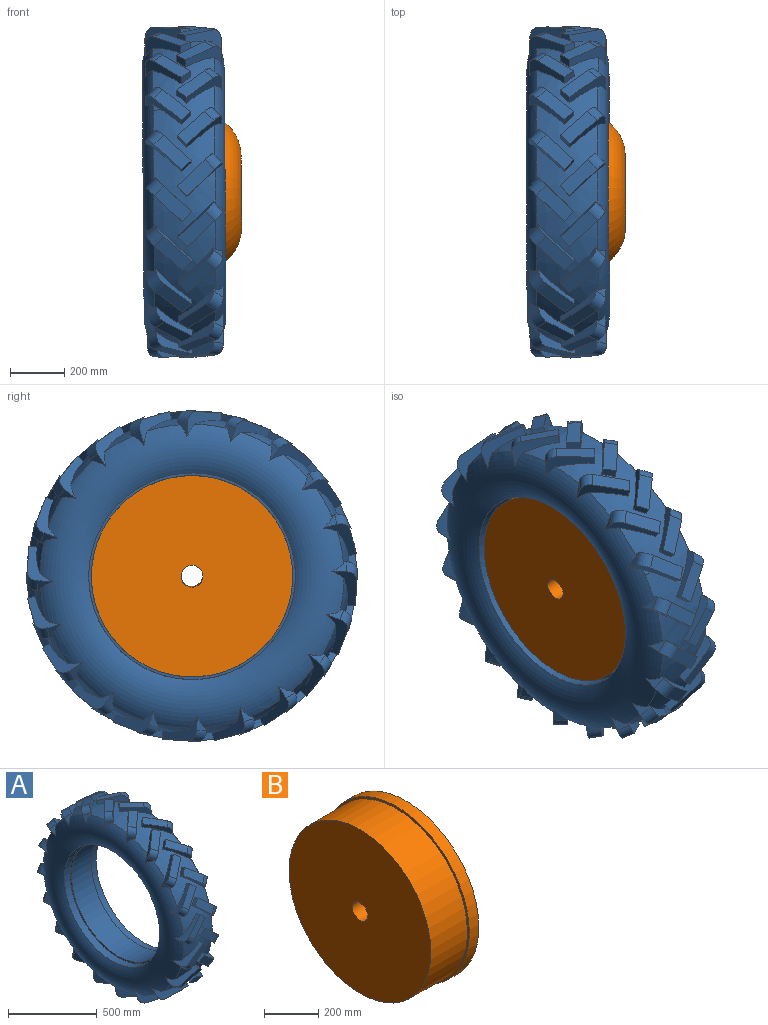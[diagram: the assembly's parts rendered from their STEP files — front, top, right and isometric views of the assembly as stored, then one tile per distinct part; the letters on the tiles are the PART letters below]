
ASSEMBLY  parts=2 mates=2
PART A: 250 faces, bbox 300.1x1226.5x1226.5 mm
  f0: torus R=460mm, axis (-1,0,0), area 542471mm2, adj f2,f4,f7,f8,f19,f20,f31,f32
  f1: cylinder r=370mm len=740mm, axis (1,0,0), area 371964.6mm2, adj f247,f249
  f2: torus R=270mm, axis (-1,0,0), area 493305.8mm2, adj f0,f3,f4,f5,f6,f7,f8,f9
  f3: torus R=270mm, axis (-1,0,0), area 381.1mm2, adj f2,f5,f195
  f4: torus R=270mm, axis (-1,0,0), area 29.1mm2, adj f0,f2,f175
  f5: torus R=460mm, axis (-1,0,0), area 542472mm2, adj f2,f3,f14,f15,f26,f27,f38,f39
  f6: plane 130.79x120.93mm, normal (0.69,0.11,-0.72), area 5311.1mm2, adj f2,f7,f9,f10,f11
  f7: plane 52.38x44.2mm, normal (-0.73,0.11,-0.68), area 1246mm2, adj f0,f2,f6,f8,f11
  f8: plane 130.8x121.4mm, normal (-0.69,-0.11,0.72), area 7014.7mm2, adj f0,f2,f7,f9,f10,f11
  f9: plane 40.79x34.46mm, normal (0.73,-0.11,0.68), area 1433.2mm2, adj f2,f6,f8,f10
  f10: plane 136.08x130.89mm, normal (0,-0.99,-0.16), area 7000mm2, adj f6,f8,f9,f11
  f11: cylinder r=40mm len=63.42mm, axis (0.69,0.11,-0.72), area 3141.6mm2, adj f6,f7,f8,f10
  f12: plane 36.44x34.46mm, normal (-0.73,0,0.69), area 1433.2mm2, adj f2,f13,f15,f16
  f13: plane 130.79x123.67mm, normal (-0.69,0,-0.73), area 5311.1mm2, adj f2,f12,f14,f16,f17
  f14: plane 53.02x36.34mm, normal (0.73,0,-0.69), area 1245.9mm2, adj f2,f5,f13,f15,f17
  f15: plane 130.79x123.67mm, normal (0.69,0,0.73), area 7014.7mm2, adj f2,f5,f12,f14,f16,f17
  f16: plane 136.08x132.52mm, normal (0,-1,0), area 7000mm2, adj f12,f13,f15,f17
  f17: cylinder r=40mm len=63.81mm, axis (-0.69,0,-0.73), area 3141.6mm2, adj f13,f14,f15,f16
  f18: plane 130.79x110.59mm, normal (0.69,0.33,-0.65), area 5311.1mm2, adj f2,f19,f21,f22,f23
  f19: plane 56.47x47.26mm, normal (-0.73,0.31,-0.61), area 1246mm2, adj f0,f2,f18,f20,f23
  f20: plane 139.03x130.8mm, normal (-0.69,-0.33,0.65), area 7014.7mm2, adj f0,f2,f19,f21,f22,f23
  f21: plane 46.41x41.26mm, normal (0.73,-0.31,0.61), area 1433.2mm2, adj f2,f18,f20,f22
  f22: plane 136.08x118.07mm, normal (0,-0.89,-0.45), area 7000mm2, adj f18,f20,f21,f23
  f23: cylinder r=40mm len=64.61mm, axis (0.69,0.33,-0.65), area 3141.6mm2, adj f18,f19,f20,f22
  f24: plane 44.15x37.65mm, normal (-0.73,-0.21,0.65), area 1433.2mm2, adj f2,f25,f27,f28
  f25: plane 130.79x116.58mm, normal (-0.69,0.22,-0.69), area 5311.1mm2, adj f2,f24,f26,f28,f29
  f26: plane 50.94x50.42mm, normal (0.73,0.21,-0.65), area 1245.9mm2, adj f2,f5,f25,f27,f29
  f27: plane 130.79x126.67mm, normal (0.69,-0.22,0.69), area 7014.7mm2, adj f2,f5,f24,f26,f28,f29
  f28: plane 136.08x126.03mm, normal (0,-0.95,-0.31), area 7000mm2, adj f24,f25,f27,f29
  f29: cylinder r=40mm len=63.42mm, axis (-0.69,0.22,-0.69), area 3141.6mm2, adj f25,f26,f27,f28
  f30: plane 130.79x122.3mm, normal (0.69,0.51,-0.51), area 5311.1mm2, adj f2,f31,f33,f34,f35
  f31: plane 63.2x37.51mm, normal (-0.73,0.49,-0.49), area 1245.9mm2, adj f0,f2,f30,f32,f35
  f32: plane 153.23x130.8mm, normal (-0.69,-0.51,0.51), area 7014.7mm2, adj f0,f2,f31,f33,f34,f35
  f33: plane 47.5x45.37mm, normal (0.73,-0.49,0.49), area 1433.2mm2, adj f2,f30,f32,f34
  f34: plane 136.08x93.7mm, normal (0,-0.71,-0.71), area 7000mm2, adj f30,f32,f33,f35
  f35: cylinder r=40mm len=73.41mm, axis (0.69,0.51,-0.51), area 3141.6mm2, adj f30,f31,f32,f34
  f36: plane 47.54x43.85mm, normal (-0.73,-0.4,0.56), area 1433.2mm2, adj f2,f37,f39,f40
  f37: plane 130.79x112.57mm, normal (-0.69,0.43,-0.59), area 5311.1mm2, adj f2,f36,f38,f40,f41
  f38: plane 60.56x42.89mm, normal (0.73,0.4,-0.56), area 1245.9mm2, adj f2,f5,f37,f39,f41
  f39: plane 147.94x130.79mm, normal (0.69,-0.43,0.59), area 7014.7mm2, adj f2,f5,f36,f38,f40,f41
  f40: plane 136.08x107.21mm, normal (0,-0.81,-0.59), area 7000mm2, adj f36,f37,f39,f41
  f41: cylinder r=40mm len=69.87mm, axis (-0.69,0.43,-0.59), area 3141.6mm2, adj f37,f38,f39,f40
  f42: plane 132.57x130.79mm, normal (0.69,0.65,-0.33), area 5311.1mm2, adj f2,f43,f45,f46,f47
  f43: plane 63.75x36.6mm, normal (-0.73,0.61,-0.31), area 1245.9mm2, adj f0,f2,f42,f44,f47
  f44: plane 152.43x130.81mm, normal (-0.69,-0.65,0.33), area 7014.7mm2, adj f0,f2,f43,f45,f46,f47
  f45: plane 45.04x43.94mm, normal (0.73,-0.61,0.31), area 1433.2mm2, adj f2,f42,f44,f46
  f46: plane 136.08x118.07mm, normal (0,-0.45,-0.89), area 7000mm2, adj f42,f44,f45,f47
  f47: cylinder r=40mm len=75.02mm, axis (0.69,0.65,-0.33), area 3141.6mm2, adj f42,f43,f44,f46
  f48: plane 46.29x45.77mm, normal (-0.73,-0.56,0.4), area 1433.2mm2, adj f2,f49,f51,f52
  f49: plane 130.79x129.02mm, normal (-0.69,0.59,-0.43), area 5311.1mm2, adj f2,f48,f50,f52,f53
  f50: plane 64.25x34.86mm, normal (0.73,0.56,-0.4), area 1245.9mm2, adj f2,f5,f49,f51,f53
  f51: plane 154.72x130.79mm, normal (0.69,-0.59,0.43), area 7014.7mm2, adj f2,f5,f48,f50,f52,f53
  f52: plane 136.08x107.21mm, normal (0,-0.59,-0.81), area 7000mm2, adj f48,f49,f51,f53
  f53: cylinder r=40mm len=75.14mm, axis (-0.69,0.59,-0.43), area 3141.6mm2, adj f49,f50,f51,f52
  f54: plane 130.79x129.86mm, normal (0.69,0.72,-0.11), area 5311.1mm2, adj f2,f55,f57,f58,f59
  f55: plane 58.07x37.35mm, normal (-0.73,0.68,-0.11), area 1245.9mm2, adj f0,f2,f54,f56,f59
  f56: plane 136.72x130.81mm, normal (-0.69,-0.72,0.11), area 7014.7mm2, adj f0,f2,f55,f57,f58,f59
  f57: plane 40.32x36.1mm, normal (0.73,-0.68,0.11), area 1433.2mm2, adj f2,f54,f56,f58
  f58: plane 136.08x130.89mm, normal (0,-0.16,-0.99), area 7000mm2, adj f54,f56,f57,f59
  f59: cylinder r=40mm len=69.28mm, axis (0.69,0.72,-0.11), area 3141.6mm2, adj f54,f55,f56,f58
  f60: plane 43.21x40.52mm, normal (-0.73,-0.65,0.21), area 1433.2mm2, adj f2,f61,f63,f64
  f61: plane 132.85x130.79mm, normal (-0.69,0.69,-0.22), area 5311.1mm2, adj f2,f60,f62,f64,f65
  f62: plane 61.65x37.43mm, normal (0.73,0.65,-0.21), area 1245.9mm2, adj f2,f5,f61,f63,f65
  f63: plane 146.36x130.79mm, normal (0.69,-0.69,0.22), area 7014.7mm2, adj f2,f5,f60,f62,f64,f65
  f64: plane 136.08x126.03mm, normal (0,-0.31,-0.95), area 7000mm2, adj f60,f61,f63,f65
  f65: cylinder r=40mm len=73.05mm, axis (-0.69,0.69,-0.22), area 3141.6mm2, adj f61,f62,f63,f64
  f66: plane 130.79x120.93mm, normal (0.69,0.72,0.11), area 5311.1mm2, adj f2,f67,f69,f70,f71
  f67: plane 52.38x44.2mm, normal (-0.73,0.68,0.11), area 1246mm2, adj f0,f2,f66,f68,f71
  f68: plane 130.8x121.4mm, normal (-0.69,-0.72,-0.11), area 7014.7mm2, adj f0,f2,f67,f69,f70,f71
  f69: plane 40.79x34.46mm, normal (0.73,-0.68,-0.11), area 1433.2mm2, adj f2,f66,f68,f70
  f70: plane 136.08x130.89mm, normal (0,0.16,-0.99), area 7000mm2, adj f66,f68,f69,f71
  f71: cylinder r=40mm len=63.42mm, axis (0.69,0.72,0.11), area 3141.6mm2, adj f66,f67,f68,f70
  f72: plane 36.44x34.46mm, normal (-0.73,-0.69,0), area 1433.2mm2, adj f2,f73,f75,f76
  f73: plane 130.79x123.67mm, normal (-0.69,0.73,0), area 5311.1mm2, adj f2,f72,f74,f76,f77
  f74: plane 53.02x36.34mm, normal (0.73,0.69,0), area 1245.9mm2, adj f2,f5,f73,f75,f77
  f75: plane 130.79x123.67mm, normal (0.69,-0.73,0), area 7014.7mm2, adj f2,f5,f72,f74,f76,f77
  f76: plane 136.08x132.52mm, normal (0,0,-1), area 7000mm2, adj f72,f73,f75,f77
  f77: cylinder r=40mm len=63.81mm, axis (-0.69,0.73,0), area 3141.6mm2, adj f73,f74,f75,f76
  f78: plane 130.79x110.59mm, normal (0.69,0.65,0.33), area 5311.1mm2, adj f2,f79,f81,f82,f83
  f79: plane 56.47x47.26mm, normal (-0.73,0.61,0.31), area 1246mm2, adj f0,f2,f78,f80,f83
  f80: plane 139.03x130.8mm, normal (-0.69,-0.65,-0.33), area 7014.7mm2, adj f0,f2,f79,f81,f82,f83
  f81: plane 46.41x41.26mm, normal (0.73,-0.61,-0.31), area 1433.2mm2, adj f2,f78,f80,f82
  f82: plane 136.08x118.07mm, normal (0,0.45,-0.89), area 7000mm2, adj f78,f80,f81,f83
  f83: cylinder r=40mm len=64.61mm, axis (0.69,0.65,0.33), area 3141.6mm2, adj f78,f79,f80,f82
  f84: plane 44.15x37.65mm, normal (-0.73,-0.65,-0.21), area 1433.2mm2, adj f2,f85,f87,f88
  f85: plane 130.79x116.58mm, normal (-0.69,0.69,0.22), area 5311.1mm2, adj f2,f84,f86,f88,f89
  f86: plane 50.94x50.42mm, normal (0.73,0.65,0.21), area 1245.9mm2, adj f2,f5,f85,f87,f89
  f87: plane 130.79x126.67mm, normal (0.69,-0.69,-0.22), area 7014.7mm2, adj f2,f5,f84,f86,f88,f89
  f88: plane 136.08x126.03mm, normal (0,0.31,-0.95), area 7000mm2, adj f84,f85,f87,f89
  f89: cylinder r=40mm len=63.42mm, axis (-0.69,0.69,0.22), area 3141.6mm2, adj f85,f86,f87,f88
  f90: plane 130.79x122.3mm, normal (0.69,0.51,0.51), area 5311.1mm2, adj f2,f91,f93,f94,f95
  f91: plane 63.2x37.51mm, normal (-0.73,0.49,0.49), area 1245.9mm2, adj f0,f2,f90,f92,f95
  f92: plane 153.23x130.8mm, normal (-0.69,-0.51,-0.51), area 7014.7mm2, adj f0,f2,f91,f93,f94,f95
  f93: plane 47.5x45.37mm, normal (0.73,-0.49,-0.49), area 1433.2mm2, adj f2,f90,f92,f94
  f94: plane 136.08x93.7mm, normal (0,0.71,-0.71), area 7000mm2, adj f90,f92,f93,f95
  f95: cylinder r=40mm len=73.41mm, axis (0.69,0.51,0.51), area 3141.6mm2, adj f90,f91,f92,f94
  f96: plane 47.54x43.85mm, normal (-0.73,-0.56,-0.4), area 1433.2mm2, adj f2,f97,f99,f100
  f97: plane 130.79x112.57mm, normal (-0.69,0.59,0.43), area 5311.1mm2, adj f2,f96,f98,f100,f101
  f98: plane 60.56x42.89mm, normal (0.73,0.56,0.4), area 1245.9mm2, adj f2,f5,f97,f99,f101
  f99: plane 147.94x130.79mm, normal (0.69,-0.59,-0.43), area 7014.7mm2, adj f2,f5,f96,f98,f100,f101
  f100: plane 136.08x107.21mm, normal (0,0.59,-0.81), area 7000mm2, adj f96,f97,f99,f101
  f101: cylinder r=40mm len=69.87mm, axis (-0.69,0.59,0.43), area 3141.6mm2, adj f97,f98,f99,f100
  f102: plane 132.57x130.79mm, normal (0.69,0.33,0.65), area 5311.1mm2, adj f2,f103,f105,f106,f107
  f103: plane 63.75x36.6mm, normal (-0.73,0.31,0.61), area 1245.9mm2, adj f0,f2,f102,f104,f107
  f104: plane 152.43x130.81mm, normal (-0.69,-0.33,-0.65), area 7014.7mm2, adj f0,f2,f103,f105,f106,f107
  f105: plane 45.04x43.94mm, normal (0.73,-0.31,-0.61), area 1433.2mm2, adj f2,f102,f104,f106
  f106: plane 136.08x118.07mm, normal (0,0.89,-0.45), area 7000mm2, adj f102,f104,f105,f107
  f107: cylinder r=40mm len=75.02mm, axis (0.69,0.33,0.65), area 3141.6mm2, adj f102,f103,f104,f106
  f108: plane 46.29x45.77mm, normal (-0.73,-0.4,-0.56), area 1433.2mm2, adj f2,f109,f111,f112
  f109: plane 130.79x129.02mm, normal (-0.69,0.43,0.59), area 5311.1mm2, adj f2,f108,f110,f112,f113
  f110: plane 64.25x34.86mm, normal (0.73,0.4,0.56), area 1245.9mm2, adj f2,f5,f109,f111,f113
  f111: plane 154.72x130.79mm, normal (0.69,-0.43,-0.59), area 7014.7mm2, adj f2,f5,f108,f110,f112,f113
  f112: plane 136.08x107.21mm, normal (0,0.81,-0.59), area 7000mm2, adj f108,f109,f111,f113
  f113: cylinder r=40mm len=75.14mm, axis (-0.69,0.43,0.59), area 3141.6mm2, adj f109,f110,f111,f112
  f114: plane 130.79x129.86mm, normal (0.69,0.11,0.72), area 5311.1mm2, adj f2,f115,f117,f118,f119
  f115: plane 58.07x37.35mm, normal (-0.73,0.11,0.68), area 1245.9mm2, adj f0,f2,f114,f116,f119
  f116: plane 136.72x130.81mm, normal (-0.69,-0.11,-0.72), area 7014.7mm2, adj f0,f2,f115,f117,f118,f119
  f117: plane 40.32x36.1mm, normal (0.73,-0.11,-0.68), area 1433.2mm2, adj f2,f114,f116,f118
  f118: plane 136.08x130.89mm, normal (0,0.99,-0.16), area 7000mm2, adj f114,f116,f117,f119
  f119: cylinder r=40mm len=69.28mm, axis (0.69,0.11,0.72), area 3141.6mm2, adj f114,f115,f116,f118
  f120: plane 43.21x40.52mm, normal (-0.73,-0.21,-0.65), area 1433.2mm2, adj f2,f121,f123,f124
  f121: plane 132.85x130.79mm, normal (-0.69,0.22,0.69), area 5311.1mm2, adj f2,f120,f122,f124,f125
  f122: plane 61.65x37.43mm, normal (0.73,0.21,0.65), area 1245.9mm2, adj f2,f5,f121,f123,f125
  f123: plane 146.36x130.79mm, normal (0.69,-0.22,-0.69), area 7014.7mm2, adj f2,f5,f120,f122,f124,f125
  f124: plane 136.08x126.03mm, normal (0,0.95,-0.31), area 7000mm2, adj f120,f121,f123,f125
  f125: cylinder r=40mm len=73.05mm, axis (-0.69,0.22,0.69), area 3141.6mm2, adj f121,f122,f123,f124
  f126: plane 130.79x120.93mm, normal (0.69,-0.11,0.72), area 5311.1mm2, adj f2,f127,f129,f130,f131
  f127: plane 52.38x44.2mm, normal (-0.73,-0.11,0.68), area 1246mm2, adj f0,f2,f126,f128,f131
  f128: plane 130.8x121.4mm, normal (-0.69,0.11,-0.72), area 7014.7mm2, adj f0,f2,f127,f129,f130,f131
  f129: plane 40.79x34.46mm, normal (0.73,0.11,-0.68), area 1433.2mm2, adj f2,f126,f128,f130
  f130: plane 136.08x130.89mm, normal (0,0.99,0.16), area 7000mm2, adj f126,f128,f129,f131
  f131: cylinder r=40mm len=63.42mm, axis (0.69,-0.11,0.72), area 3141.6mm2, adj f126,f127,f128,f130
  f132: plane 36.44x34.46mm, normal (-0.73,0,-0.69), area 1433.2mm2, adj f2,f133,f135,f136
  f133: plane 130.79x123.67mm, normal (-0.69,0,0.73), area 5311.1mm2, adj f2,f132,f134,f136,f137
  f134: plane 53.02x36.34mm, normal (0.73,0,0.69), area 1245.9mm2, adj f2,f5,f133,f135,f137
  f135: plane 130.79x123.67mm, normal (0.69,0,-0.73), area 7014.7mm2, adj f2,f5,f132,f134,f136,f137
  f136: plane 136.08x132.52mm, normal (0,1,0), area 7000mm2, adj f132,f133,f135,f137
  f137: cylinder r=40mm len=63.81mm, axis (-0.69,0,0.73), area 3141.6mm2, adj f133,f134,f135,f136
  f138: plane 130.79x110.59mm, normal (0.69,-0.33,0.65), area 5311.1mm2, adj f2,f139,f141,f142,f143
  f139: plane 56.47x47.26mm, normal (-0.73,-0.31,0.61), area 1246mm2, adj f0,f2,f138,f140,f143
  f140: plane 139.03x130.8mm, normal (-0.69,0.33,-0.65), area 7014.7mm2, adj f0,f2,f139,f141,f142,f143
  f141: plane 46.41x41.26mm, normal (0.73,0.31,-0.61), area 1433.2mm2, adj f2,f138,f140,f142
  f142: plane 136.08x118.07mm, normal (0,0.89,0.45), area 7000mm2, adj f138,f140,f141,f143
  f143: cylinder r=40mm len=64.61mm, axis (0.69,-0.33,0.65), area 3141.6mm2, adj f138,f139,f140,f142
  f144: plane 44.15x37.65mm, normal (-0.73,0.21,-0.65), area 1433.2mm2, adj f2,f145,f147,f148
  f145: plane 130.79x116.58mm, normal (-0.69,-0.22,0.69), area 5311.1mm2, adj f2,f144,f146,f148,f149
  f146: plane 50.94x50.42mm, normal (0.73,-0.21,0.65), area 1245.9mm2, adj f2,f5,f145,f147,f149
  f147: plane 130.79x126.67mm, normal (0.69,0.22,-0.69), area 7014.7mm2, adj f2,f5,f144,f146,f148,f149
  f148: plane 136.08x126.03mm, normal (0,0.95,0.31), area 7000mm2, adj f144,f145,f147,f149
  f149: cylinder r=40mm len=63.42mm, axis (-0.69,-0.22,0.69), area 3141.6mm2, adj f145,f146,f147,f148
  f150: plane 130.79x122.3mm, normal (0.69,-0.51,0.51), area 5311.1mm2, adj f2,f151,f153,f154,f155
  f151: plane 63.2x37.51mm, normal (-0.73,-0.49,0.49), area 1245.9mm2, adj f0,f2,f150,f152,f155
  f152: plane 153.23x130.8mm, normal (-0.69,0.51,-0.51), area 7014.7mm2, adj f0,f2,f151,f153,f154,f155
  f153: plane 47.5x45.37mm, normal (0.73,0.49,-0.49), area 1433.2mm2, adj f2,f150,f152,f154
  f154: plane 136.08x93.7mm, normal (0,0.71,0.71), area 7000mm2, adj f150,f152,f153,f155
  f155: cylinder r=40mm len=73.41mm, axis (0.69,-0.51,0.51), area 3141.6mm2, adj f150,f151,f152,f154
  f156: plane 47.54x43.85mm, normal (-0.73,0.4,-0.56), area 1433.2mm2, adj f2,f157,f159,f160
  f157: plane 130.79x112.57mm, normal (-0.69,-0.43,0.59), area 5311.1mm2, adj f2,f156,f158,f160,f161
  f158: plane 60.56x42.89mm, normal (0.73,-0.4,0.56), area 1245.9mm2, adj f2,f5,f157,f159,f161
  f159: plane 147.94x130.79mm, normal (0.69,0.43,-0.59), area 7014.7mm2, adj f2,f5,f156,f158,f160,f161
  f160: plane 136.08x107.21mm, normal (0,0.81,0.59), area 7000mm2, adj f156,f157,f159,f161
  f161: cylinder r=40mm len=69.87mm, axis (-0.69,-0.43,0.59), area 3141.6mm2, adj f157,f158,f159,f160
  f162: plane 132.57x130.79mm, normal (0.69,-0.65,0.33), area 5311.1mm2, adj f2,f163,f165,f166,f167
  f163: plane 63.75x36.6mm, normal (-0.73,-0.61,0.31), area 1245.9mm2, adj f0,f2,f162,f164,f167
  f164: plane 152.43x130.81mm, normal (-0.69,0.65,-0.33), area 7014.7mm2, adj f0,f2,f163,f165,f166,f167
  f165: plane 45.04x43.94mm, normal (0.73,0.61,-0.31), area 1433.2mm2, adj f2,f162,f164,f166
  f166: plane 136.08x118.07mm, normal (0,0.45,0.89), area 7000mm2, adj f162,f164,f165,f167
  f167: cylinder r=40mm len=75.02mm, axis (0.69,-0.65,0.33), area 3141.6mm2, adj f162,f163,f164,f166
  f168: plane 46.29x45.77mm, normal (-0.73,0.56,-0.4), area 1433.2mm2, adj f2,f169,f171,f172
  f169: plane 130.79x129.02mm, normal (-0.69,-0.59,0.43), area 5311.1mm2, adj f2,f168,f170,f172,f173
  f170: plane 64.25x34.86mm, normal (0.73,-0.56,0.4), area 1245.9mm2, adj f2,f5,f169,f171,f173
  f171: plane 154.72x130.79mm, normal (0.69,0.59,-0.43), area 7014.7mm2, adj f2,f5,f168,f170,f172,f173
  f172: plane 136.08x107.21mm, normal (0,0.59,0.81), area 7000mm2, adj f168,f169,f171,f173
  f173: cylinder r=40mm len=75.14mm, axis (-0.69,-0.59,0.43), area 3141.6mm2, adj f169,f170,f171,f172
  f174: plane 130.79x129.86mm, normal (0.69,-0.72,0.11), area 5311.1mm2, adj f2,f175,f177,f178,f179
  f175: plane 58.07x37.35mm, normal (-0.73,-0.68,0.11), area 1245.9mm2, adj f0,f4,f174,f176,f179
  f176: plane 136.72x130.81mm, normal (-0.69,0.72,-0.11), area 7014.7mm2, adj f0,f2,f175,f177,f178,f179
  f177: plane 40.32x36.1mm, normal (0.73,0.68,-0.11), area 1433.2mm2, adj f2,f174,f176,f178
  f178: plane 136.08x130.89mm, normal (0,0.16,0.99), area 7000mm2, adj f174,f176,f177,f179
  f179: cylinder r=40mm len=69.28mm, axis (0.69,-0.72,0.11), area 3141.6mm2, adj f174,f175,f176,f178
  f180: plane 43.21x40.52mm, normal (-0.73,0.65,-0.21), area 1433.2mm2, adj f2,f181,f183,f184
  f181: plane 132.85x130.79mm, normal (-0.69,-0.69,0.22), area 5311.1mm2, adj f2,f180,f182,f184,f185
  f182: plane 61.65x37.43mm, normal (0.73,-0.65,0.21), area 1245.9mm2, adj f2,f5,f181,f183,f185
  f183: plane 146.36x130.79mm, normal (0.69,0.69,-0.22), area 7014.7mm2, adj f2,f5,f180,f182,f184,f185
  f184: plane 136.08x126.03mm, normal (0,0.31,0.95), area 7000mm2, adj f180,f181,f183,f185
  f185: cylinder r=40mm len=73.05mm, axis (-0.69,-0.69,0.22), area 3141.6mm2, adj f181,f182,f183,f184
  f186: plane 130.79x120.93mm, normal (0.69,-0.72,-0.11), area 5311.1mm2, adj f2,f187,f189,f190,f191
  f187: plane 52.38x44.2mm, normal (-0.73,-0.68,-0.11), area 1246mm2, adj f0,f2,f186,f188,f191
  f188: plane 130.8x121.4mm, normal (-0.69,0.72,0.11), area 7014.7mm2, adj f0,f2,f187,f189,f190,f191
  f189: plane 40.79x34.46mm, normal (0.73,0.68,0.11), area 1433.2mm2, adj f2,f186,f188,f190
  f190: plane 136.08x130.89mm, normal (0,-0.16,0.99), area 7000mm2, adj f186,f188,f189,f191
  f191: cylinder r=40mm len=63.42mm, axis (0.69,-0.72,-0.11), area 3141.6mm2, adj f186,f187,f188,f190
  f192: plane 36.44x34.46mm, normal (-0.73,0.69,0), area 1433.2mm2, adj f2,f193,f195,f196
  f193: plane 130.79x123.67mm, normal (-0.69,-0.73,0), area 5311.1mm2, adj f2,f192,f194,f196,f197
  f194: plane 53.02x36.34mm, normal (0.73,-0.69,0), area 1245.9mm2, adj f2,f5,f193,f195,f197
  f195: plane 130.79x123.67mm, normal (0.69,0.73,0), area 7014.7mm2, adj f2,f3,f5,f192,f194,f196,f197
  f196: plane 136.08x132.52mm, normal (0,0,1), area 7000mm2, adj f192,f193,f195,f197
  f197: cylinder r=40mm len=63.81mm, axis (-0.69,-0.73,0), area 3141.6mm2, adj f193,f194,f195,f196
  f198: plane 130.79x110.59mm, normal (0.69,-0.65,-0.33), area 5311.1mm2, adj f2,f199,f201,f202,f203
  f199: plane 56.47x47.26mm, normal (-0.73,-0.61,-0.31), area 1246mm2, adj f0,f2,f198,f200,f203
  f200: plane 139.03x130.8mm, normal (-0.69,0.65,0.33), area 7014.7mm2, adj f0,f2,f199,f201,f202,f203
  f201: plane 46.41x41.26mm, normal (0.73,0.61,0.31), area 1433.2mm2, adj f2,f198,f200,f202
  f202: plane 136.08x118.07mm, normal (0,-0.45,0.89), area 7000mm2, adj f198,f200,f201,f203
  f203: cylinder r=40mm len=64.61mm, axis (0.69,-0.65,-0.33), area 3141.6mm2, adj f198,f199,f200,f202
  f204: plane 44.15x37.65mm, normal (-0.73,0.65,0.21), area 1433.2mm2, adj f2,f205,f207,f208
  f205: plane 130.79x116.58mm, normal (-0.69,-0.69,-0.22), area 5311.1mm2, adj f2,f204,f206,f208,f209
  f206: plane 50.94x50.42mm, normal (0.73,-0.65,-0.21), area 1245.9mm2, adj f2,f5,f205,f207,f209
  f207: plane 130.79x126.67mm, normal (0.69,0.69,0.22), area 7014.7mm2, adj f2,f5,f204,f206,f208,f209
  f208: plane 136.08x126.03mm, normal (0,-0.31,0.95), area 7000mm2, adj f204,f205,f207,f209
  f209: cylinder r=40mm len=63.42mm, axis (-0.69,-0.69,-0.22), area 3141.6mm2, adj f205,f206,f207,f208
  f210: plane 130.79x122.3mm, normal (0.69,-0.51,-0.51), area 5311.1mm2, adj f2,f211,f213,f214,f215
  f211: plane 63.2x37.51mm, normal (-0.73,-0.49,-0.49), area 1245.9mm2, adj f0,f2,f210,f212,f215
  f212: plane 153.23x130.8mm, normal (-0.69,0.51,0.51), area 7014.7mm2, adj f0,f2,f211,f213,f214,f215
  f213: plane 47.5x45.37mm, normal (0.73,0.49,0.49), area 1433.2mm2, adj f2,f210,f212,f214
  f214: plane 136.08x93.7mm, normal (0,-0.71,0.71), area 7000mm2, adj f210,f212,f213,f215
  f215: cylinder r=40mm len=73.41mm, axis (0.69,-0.51,-0.51), area 3141.6mm2, adj f210,f211,f212,f214
  f216: plane 47.54x43.85mm, normal (-0.73,0.56,0.4), area 1433.2mm2, adj f2,f217,f219,f220
  f217: plane 130.79x112.57mm, normal (-0.69,-0.59,-0.43), area 5311.1mm2, adj f2,f216,f218,f220,f221
  f218: plane 60.56x42.89mm, normal (0.73,-0.56,-0.4), area 1245.9mm2, adj f2,f5,f217,f219,f221
  f219: plane 147.94x130.79mm, normal (0.69,0.59,0.43), area 7014.7mm2, adj f2,f5,f216,f218,f220,f221
  f220: plane 136.08x107.21mm, normal (0,-0.59,0.81), area 7000mm2, adj f216,f217,f219,f221
  f221: cylinder r=40mm len=69.87mm, axis (-0.69,-0.59,-0.43), area 3141.6mm2, adj f217,f218,f219,f220
  f222: plane 132.57x130.79mm, normal (0.69,-0.33,-0.65), area 5311.1mm2, adj f2,f223,f225,f226,f227
  f223: plane 63.75x36.6mm, normal (-0.73,-0.31,-0.61), area 1245.9mm2, adj f0,f2,f222,f224,f227
  f224: plane 152.43x130.81mm, normal (-0.69,0.33,0.65), area 7014.7mm2, adj f0,f2,f223,f225,f226,f227
  f225: plane 45.04x43.94mm, normal (0.73,0.31,0.61), area 1433.2mm2, adj f2,f222,f224,f226
  f226: plane 136.08x118.07mm, normal (0,-0.89,0.45), area 7000mm2, adj f222,f224,f225,f227
  f227: cylinder r=40mm len=75.02mm, axis (0.69,-0.33,-0.65), area 3141.6mm2, adj f222,f223,f224,f226
  f228: plane 46.29x45.77mm, normal (-0.73,0.4,0.56), area 1433.2mm2, adj f2,f229,f231,f232
  f229: plane 130.79x129.02mm, normal (-0.69,-0.43,-0.59), area 5311.1mm2, adj f2,f228,f230,f232,f233
  f230: plane 64.25x34.86mm, normal (0.73,-0.4,-0.56), area 1245.9mm2, adj f2,f5,f229,f231,f233
  f231: plane 154.72x130.79mm, normal (0.69,0.43,0.59), area 7014.7mm2, adj f2,f5,f228,f230,f232,f233
  f232: plane 136.08x107.21mm, normal (0,-0.81,0.59), area 7000mm2, adj f228,f229,f231,f233
  f233: cylinder r=40mm len=75.14mm, axis (-0.69,-0.43,-0.59), area 3141.6mm2, adj f229,f230,f231,f232
  f234: plane 130.79x129.86mm, normal (0.69,-0.11,-0.72), area 5311.1mm2, adj f2,f235,f237,f238,f239
  f235: plane 58.07x37.35mm, normal (-0.73,-0.11,-0.68), area 1245.9mm2, adj f0,f2,f234,f236,f239
  f236: plane 136.72x130.81mm, normal (-0.69,0.11,0.72), area 7014.7mm2, adj f0,f2,f235,f237,f238,f239
  f237: plane 40.32x36.1mm, normal (0.73,0.11,0.68), area 1433.2mm2, adj f2,f234,f236,f238
  f238: plane 136.08x130.89mm, normal (0,-0.99,0.16), area 7000mm2, adj f234,f236,f237,f239
  f239: cylinder r=40mm len=69.28mm, axis (0.69,-0.11,-0.72), area 3141.6mm2, adj f234,f235,f236,f238
  f240: plane 43.21x40.52mm, normal (-0.73,0.21,0.65), area 1433.2mm2, adj f2,f241,f243,f244
  f241: plane 132.85x130.79mm, normal (-0.69,-0.22,-0.69), area 5311.1mm2, adj f2,f240,f242,f244,f245
  f242: plane 61.65x37.43mm, normal (0.73,-0.21,-0.65), area 1245.9mm2, adj f2,f5,f241,f243,f245
  f243: plane 146.36x130.79mm, normal (0.69,0.22,0.69), area 7014.7mm2, adj f2,f5,f240,f242,f244,f245
  f244: plane 136.08x126.03mm, normal (0,-0.95,0.31), area 7000mm2, adj f240,f241,f243,f245
  f245: cylinder r=40mm len=73.05mm, axis (-0.69,-0.22,-0.69), area 3141.6mm2, adj f241,f242,f243,f244
  f246: cylinder r=380mm len=760mm, axis (1,0,0), area 111945mm2, adj f5,f247
  f247: plane 760x760mm, normal (1,0,0), area 23561.9mm2, adj f1,f246
  f248: cylinder r=380mm len=760mm, axis (-1,0,0), area 111945mm2, adj f0,f249
  f249: plane 760x760mm, normal (-1,0,0), area 23561.9mm2, adj f1,f248
PART B: 12 faces, bbox 320x768.5x768.5 mm
  f0: cylinder r=380mm len=760mm, axis (1,0,0), area 119380.5mm2, adj f1,f2
  f1: plane 760x760mm, normal (-1,0,0), area 23561.9mm2, adj f0,f3
  f2: plane 760x760mm, normal (1,0,0), area 57726.8mm2, adj f0,f11
  f3: cylinder r=370mm len=740mm, axis (1,0,0), area 441707.9mm2, adj f1,f4
  f4: plane 740x740mm, normal (-1,0,0), area 425057.5mm2, adj f3,f7
  f5: plane 262.87x262.87mm, normal (1,0,0), area 49245.7mm2, adj f6,f7
  f6: torus R=131.44mm, axis (-1,0,0), area 218795mm2, adj f5,f9
  f7: cylinder r=40mm len=320mm, axis (-1,0,0), area 80424.8mm2, adj f4,f5
  f8: cylinder r=330mm len=660mm, axis (1,0,0), area 72570.8mm2, adj f10,f11
  f9: cylinder r=270mm len=540mm, axis (1,0,0), area 101787.6mm2, adj f6,f10
  f10: plane 660x660mm, normal (1,0,0), area 113097.3mm2, adj f8,f9
  f11: torus R=355mm, axis (1,0,0), area 83665.7mm2, adj f2,f8
PLACE A rot(axis=(0,0.48,-0.88),179.7deg) t=(-112.04,-2550.96,3145.48)mm
PLACE B rot(axis=(-1,0,0),123.3deg) t=(17.96,-2550.72,3146.4)mm
MATE planar B.f0 <-> A.f0  axis (-1,0,-0.01) through (-32.04,-2550.81,3146.05)mm
MATE cylindrical B.f3 <-> A.f0  axis (1,0,0.01) through (-127.04,-2550.98,3145.37)mm
